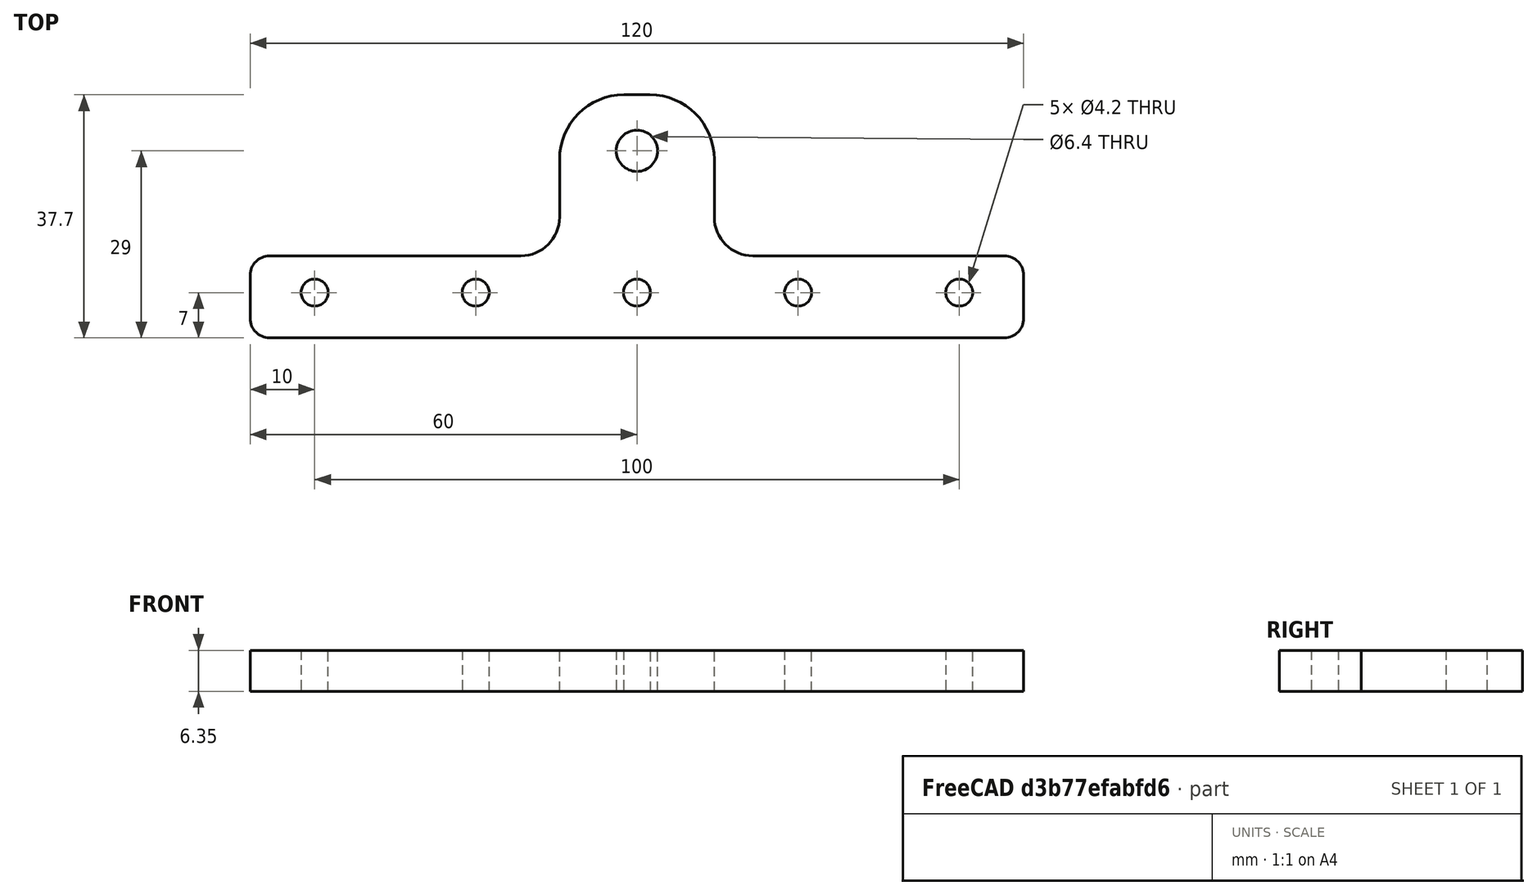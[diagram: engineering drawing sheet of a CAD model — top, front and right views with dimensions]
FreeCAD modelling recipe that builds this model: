
FCSTD DOCUMENT  (FreeCAD 0.19R)
Label: BedSupport120mm
License: All rights reserved
LicenseURL: http://en.wikipedia.org/wiki/All_rights_reserved
objects: Sketcher::SketchObject×1, PartDesign::Pad×1, PartDesign::Body×1, Mesh::Feature×1
note: 4 computed .brp shape members not serialized (recipe doc carries the construction recipe); baked Part::Feature solids carry a one-line shape summary decoded from their .brp

FEATURE [Sketcher::SketchObject] Sketch023
  FullyConstrained = false
  sketch-geometry (22):
    g0: LineSegment StartX=-60 StartY=3 StartZ=0 EndX=-60 EndY=9.7 EndZ=0
    g1: LineSegment StartX=-57 StartY=0 StartZ=0 EndX=57 EndY=0 EndZ=0
    g2: LineSegment StartX=18 StartY=12.7 StartZ=0 EndX=57 EndY=12.7 EndZ=0
    g3: LineSegment StartX=60 StartY=3 StartZ=0 EndX=60 EndY=9.7 EndZ=0
    g4: LineSegment StartX=-57 StartY=12.7 StartZ=0 EndX=-18 EndY=12.7 EndZ=0
    g5: LineSegment StartX=-12 StartY=18.7 StartZ=0 EndX=-12 EndY=27.7 EndZ=0
    g6: LineSegment StartX=-2 StartY=37.7 StartZ=0 EndX=2 EndY=37.7 EndZ=0
    g7: LineSegment StartX=12 StartY=18.7 StartZ=0 EndX=12 EndY=27.7 EndZ=0
    g8: ArcOfCircle CenterX=18 CenterY=18.7 CenterZ=0 NormalX=0 NormalY=0 NormalZ=1 AngleXU=0 Radius=6 StartAngle=3.14159 EndAngle=4.71239
    g9: ArcOfCircle CenterX=-18 CenterY=18.7 CenterZ=0 NormalX=0 NormalY=0 NormalZ=1 AngleXU=0 Radius=6 StartAngle=4.71239 EndAngle=6.28319
    g10: ArcOfCircle CenterX=57 CenterY=3 CenterZ=0 NormalX=0 NormalY=0 NormalZ=1 AngleXU=0 Radius=3 StartAngle=4.71239 EndAngle=6.28319
    g11: ArcOfCircle CenterX=57 CenterY=9.7 CenterZ=0 NormalX=0 NormalY=0 NormalZ=1 AngleXU=0 Radius=3 StartAngle=0 EndAngle=1.5708
    g12: ArcOfCircle CenterX=-57 CenterY=9.7 CenterZ=0 NormalX=0 NormalY=0 NormalZ=1 AngleXU=0 Radius=3 StartAngle=1.5708 EndAngle=3.14159
    g13: ArcOfCircle CenterX=-57 CenterY=3 CenterZ=0 NormalX=0 NormalY=0 NormalZ=1 AngleXU=0 Radius=3 StartAngle=3.14159 EndAngle=4.71239
    g14: ArcOfCircle CenterX=2 CenterY=27.7 CenterZ=0 NormalX=0 NormalY=0 NormalZ=1 AngleXU=0 Radius=10 StartAngle=0 EndAngle=1.5708
    g15: ArcOfCircle CenterX=-2 CenterY=27.7 CenterZ=0 NormalX=0 NormalY=0 NormalZ=1 AngleXU=0 Radius=10 StartAngle=1.5708 EndAngle=3.14159
    g16: Circle CenterX=0 CenterY=7 CenterZ=0 NormalX=0 NormalY=0 NormalZ=1 AngleXU=0 Radius=2.1
    g17: Circle CenterX=50 CenterY=7 CenterZ=0 NormalX=0 NormalY=0 NormalZ=1 AngleXU=0 Radius=2.1
    g18: Circle CenterX=-50 CenterY=7 CenterZ=0 NormalX=0 NormalY=0 NormalZ=1 AngleXU=0 Radius=2.1
    g19: Circle CenterX=25 CenterY=7 CenterZ=0 NormalX=0 NormalY=0 NormalZ=1 AngleXU=0 Radius=2.1
    g20: Circle CenterX=-25 CenterY=7 CenterZ=0 NormalX=0 NormalY=0 NormalZ=1 AngleXU=0 Radius=2.1
    g21: Circle CenterX=0 CenterY=29 CenterZ=0 NormalX=0 NormalY=0 NormalZ=1 AngleXU=0 Radius=3.2
  constraints (16):
    c: Coincident(g0,g13)
    c: Coincident(g0,g12)
    c: Coincident(g1,g13)
    c: Coincident(g12,g4)
    c: Coincident(g4,g9)
    c: Coincident(g5,g9)
    c: Coincident(g15,g5)
    c: Coincident(g6,g15)
    c: Coincident(g6,g14)
    c: Coincident(g7,g8)
    c: Coincident(g7,g14)
    c: Coincident(g8,g2)
    c: Coincident(g1,g10)
    c: Coincident(g2,g11)
    c: Coincident(g3,g10)
    c: Coincident(g3,g11)
FEATURE [PartDesign::Pad] Pad
  Direction = (1,1,1)
  Length = 6.35
  Length2 = 100
  Profile = -> Sketch023
  Type = 0
FEATURE [PartDesign::Body] Body
  Group = -> [Sketch023,Pad]
  Origin = -> Origin
  Tip = -> Pad
FEATURE [Mesh::Feature] Mesh  label="Pad (Meshed)"
